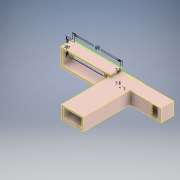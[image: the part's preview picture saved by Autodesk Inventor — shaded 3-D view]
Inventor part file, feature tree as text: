
AUTODESK INVENTOR PART (.ipt)
format: ipt  version: 2020 (Build 240168000, 168)  size: 447,488 bytes
history: native  units: mm
features: extrude x26, sketch x24, pattern_linear x3, other x2
ambient origin geometry x8: Origin, YZ Plane, XZ Plane, XY Plane, X Axis, Y Axis, Z Axis, Center Point
bodies: Solid1 (feature_tree)
feature tree (55):
  extrude  "Extrusion1"  Depth=11.0mm
  extrude  "Extrusion2"  Depth=15.0mm
  sketch  "Sketch3"  dims[d4=70.0mm d5=0.0mm d7=1.0mm]
  extrude  "Extrusion3"  Depth=1.0mm
  sketch  "Sketch4"  dims[d8=1.0mm d9=6.0mm]
  extrude  "Extrusion4"  Depth=6.0mm
  extrude  "Extrusion5"  Depth=1.0mm
  extrude  "Extrusion6"  Depth=55.0mm
  extrude  "Extrusion7"  Depth=21.0mm
  extrude  "Extrusion8"  Depth=4.0mm
  extrude  "Extrusion9"  Depth=14.0mm TaperAngle=0.0deg
  extrude  "Extrusion10"  Depth=3.5mm
  extrude  "Extrusion11"  Depth=14.0mm TaperAngle=0.0deg
  extrude  "Extrusion12"  Depth=11.0mm
  extrude  "Extrusion13"  Depth=22.0mm TaperAngle=0.0deg
  extrude  "Extrusion14"  Depth=7.0mm
  extrude  "Extrusion15"  Depth=3.0mm
  extrude  "Extrusion16"  Depth=11.0mm TaperAngle=0.0deg
  extrude  "Extrusion17"  Depth=2.0mm
  extrude  "Extrusion18"  Depth=2.0mm
  extrude  "Extrusion19"  Depth=2.0mm TaperAngle=0.0deg
  extrude  "Extrusion20"  Depth=2.0mm
  extrude  "Extrusion21"  Depth=7.0mm TaperAngle=0.0deg
  extrude  "Extrusion22"  Depth=7.0mm TaperAngle=0.0deg
  extrude  "Extrusion23"  Depth=10.0mm
  pattern_linear  "Rectangular Pattern1"  Spacing1=2.0mm  [1 undecoded]
  pattern_linear  "Rectangular Pattern2"  Spacing1=2.0mm  [1 undecoded]
  extrude  "Extrusion24"  Depth=13.0mm
  pattern_linear  "Rectangular Pattern3"  Spacing1=2.0mm  [1 undecoded]
  extrude  "Extrusion25"  Depth=2.0mm TaperAngle=0.0deg
  extrude  "Extrusion27"  Depth=2.0mm TaperAngle=0.0deg
  sketch  "Sketch1"  dims[d0=22.0mm d1=11.0mm]
  sketch  "Sketch2"  dims[d2=26.0mm d3=15.0mm]
  sketch  "Sketch5"  dims[d10=2.0mm d11=0.0mm d12=1.0mm]
  sketch  "Sketch6"  dims[d14=17.0mm d15=55.0mm]
  sketch  "Sketch7"  dims[d19=3.0mm d21=21.0mm]
  sketch  "Sketch8"  dims[d22=59.0mm d23=4.0mm]
  sketch  "Sketch9"  dims[d24=6.0mm d25=14.0mm d26=0.0mm]
  sketch  "Sketch10"  dims[d27=3.5mm d28=0.0mm d29=3.5mm]
  sketch  "Sketch11"  dims[d30=3.5mm d31=14.0mm d32=0.0mm]
  sketch  "Sketch12"  dims[d33=14.0mm d34=0.0mm d39=11.0mm]
  sketch  "Sketch13"  dims[d40=2.0mm d41=22.0mm d42=0.0mm]
  sketch  "Sketch14"  dims[d45=2.0mm d46=7.0mm]
  sketch  "Sketch15"  dims[d48=2.0mm d49=0.0mm d50=3.0mm]
  sketch  "Sketch16"  dims[d51=1.5mm d52=11.0mm d53=0.0mm]
  sketch  "Sketch17"  dims[d58=37.0mm d59=0.0mm d60=2.0mm]
  sketch  "Sketch18"  dims[d61=13.0mm d62=0.0mm d63=2.0mm]
  sketch  "Sketch19"  dims[d64=2.0mm d65=83.0mm d66=0.0mm]
  sketch  "Sketch20"  dims[d67=42.0mm d68=0.0mm d70=2.0mm]
  sketch  "Sketch21"  dims[d71=15.0mm d72=0.0mm d73=7.0mm d74=0.0mm]
  sketch  "Sketch22"  dims[d75=2.0mm d76=7.0mm d77=0.0mm]
  sketch  "Sketch23"  dims[d78=5.0mm d79=0.0mm d80=10.0mm]
  sketch  "Sketch25"  dims[d81=10.0mm d82=2.0mm d83=0.0mm d84=2.0mm d85=13.0mm d86=2.0mm d87=0.0mm d88=2.0mm d89=0.0mm d90=2.0mm d91=0.0mm d92=5.0mm d93=0.0mm d96=2.4mm d97=2.0mm d98=0.0mm d99=20.0mm d101=30.0mm d102=30.0mm d104=25.0mm d107=2.4mm d108=2.0mm d109=0.0mm d110=20.0mm d112=20.0mm d113=30.0mm d115=30.0mm d116=35.0mm d117=0.0mm d120=25.0mm d121=0.0mm d35=0.5mm d36=0.872665mm d69=0.5mm]
  other  "Composite1"
  other  "Srf1"
note: 3 required parameter values undecoded (feature->parameter linkage not recoverable at this tier; creation-order binding heuristic only, values carry confidence <= 0.55)
